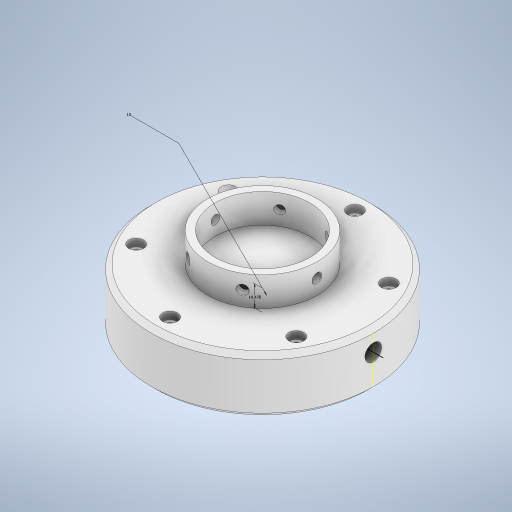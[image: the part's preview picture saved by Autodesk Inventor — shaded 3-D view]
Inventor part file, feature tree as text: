
AUTODESK INVENTOR PART (.ipt)
format: ipt  version: 2023 (Build 270158030, 158C)  size: 446,464 bytes
history: native  units: in
note: dims shown in document units (in); Inventor stores cm internally (conversion verified against a paired STEP export)
features: sketch x11, hole x4, plane x3, extrude x2, pattern_circular x2, sweep x2, other x1, chamfer x1, projected_geometry x1
ambient origin geometry x8: Origin, YZ Plane, XZ Plane, XY Plane, X Axis, Y Axis, Z Axis, Center Point
bodies: Solid1 (feature_tree)
feature tree (27):
  extrude  "Main Body"  Depth=1.5in TaperAngle=0.0deg
  hole  "M5 Bolt"  [1 undecoded]
  pattern_circular  "Circular Pattern1"  Count=6 Angle=360.0deg
  other  "Membrane Cutout"
  chamfer  "Chamfer1"  Distance=0.125in Angle=45.0deg
  sketch  "Sketch5"  dims[d15=0.11in]
  plane  "Work Plane1"
  sweep  "Sweep2"
  hole  "Hole4"  [1 undecoded]
  extrude  "Extrusion2"  Depth=0.1969in
  plane  "Work Plane2"
  hole  "Hole5"  [1 undecoded]
  pattern_circular  "Circular Pattern2"  [2 undecoded]
  sketch  "Sketch12"  dims[d33=0.125in d45=0.1in]
  plane  "Work Plane3"
  sweep  "Sweep3"
  hole  "Hole6"  [1 undecoded]
  sketch  "Sketch1"  dims[d0=6.0in d1=1.5in d2=0.0in]
  sketch  "Sketch2"  dims[d3=0.209in d4=0.75in d5=0.4in d6=0.2in d7=0.5635in d8=0.9798in d9=0.0in d10=2.5in d11=2.3622in d12=360.0deg]
  sketch  "Sketch3"  dims[d14=2.25in]
  sketch  "Sketch7"  dims[d17=360.0deg]
  sketch  "Sketch9"  dims[d18=0.5in]
  sketch  "Sketch10"  dims[d19=0.5in]
  sketch  "Sketch11"  dims[d20=2.25in d30=0.125in d31=0.125in d32=45.0deg]
  projected_geometry  "Projected Loop1"
  sketch  "Sketch13"  dims[d46=0.0in d47=0.0in]
  sketch  "Sketch14"  dims[d48=0.25in d49=0.5in d50=0.0246in d51=0.426in d52=0.375in d53=0.25in d54=0.5635in d55=0.26in d56=0.8108in d57=2.5591in d58=0.1969in d59=0.7874in d60=0.0in d61=0.2362in d62=0.2362in d63=0.2756in d64=0.0787in d65=90.0deg d66=0.6167in d67=0.8108in d68=0.3937in d69=2.3622in d70=360.0deg d72=0.57in d73=0.3937in d74=0.0in d75=0.0in d76=0.3937in d77=0.422in d78=0.3389in d79=0.2756in d80=0.0787in d81=90.0deg d82=0.3543in d83=0.8108in d84=0.0246in d85=0.426in]
note: 6 required parameter values undecoded (feature->parameter linkage not recoverable at this tier; creation-order binding heuristic only, values carry confidence <= 0.55)
